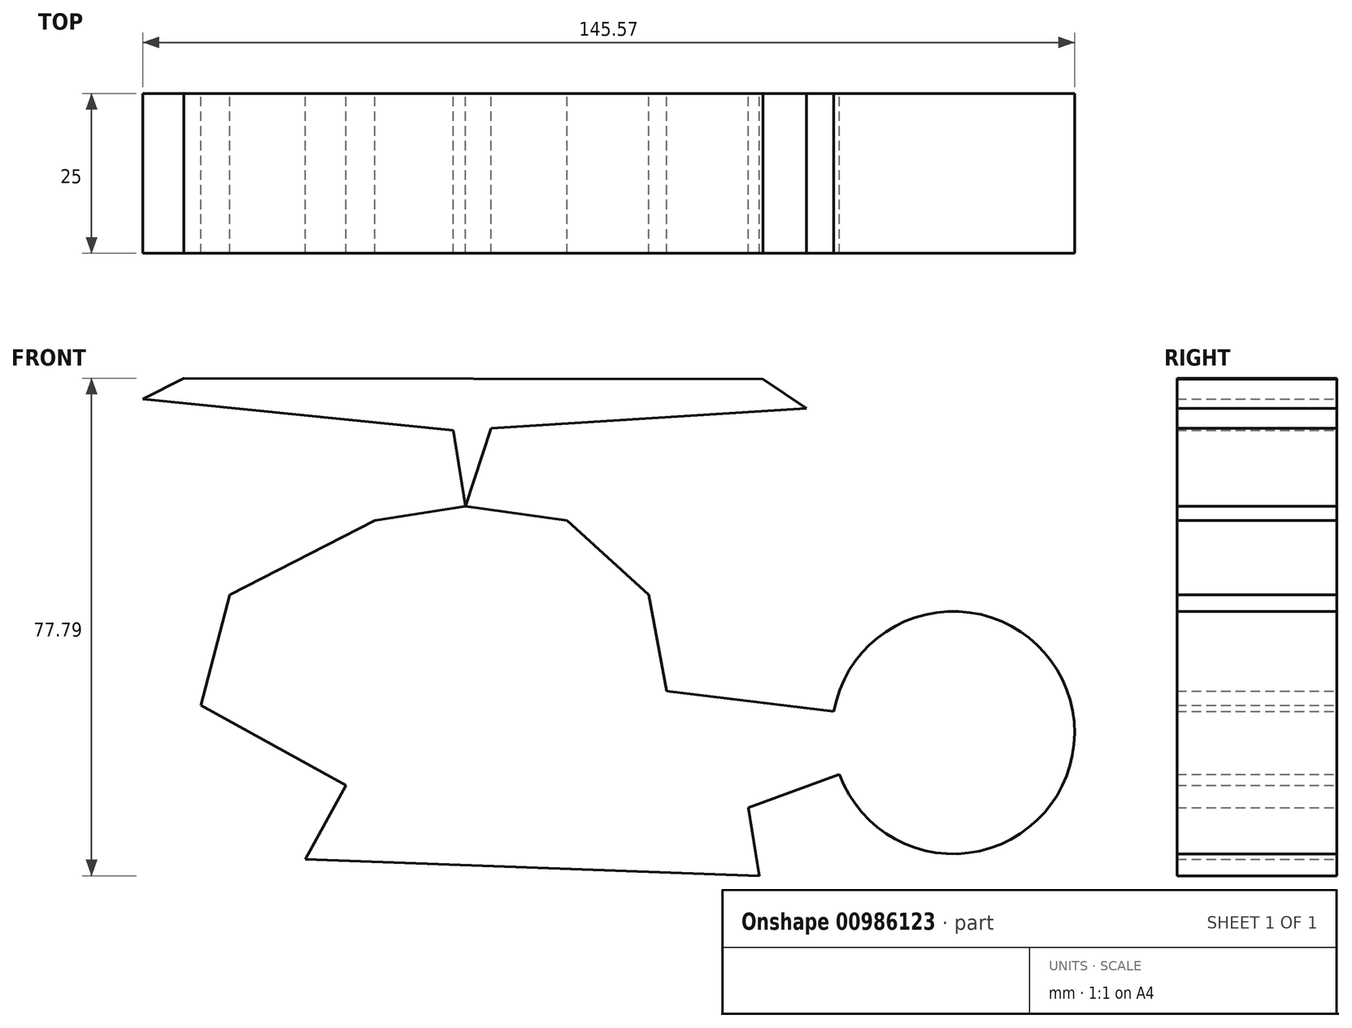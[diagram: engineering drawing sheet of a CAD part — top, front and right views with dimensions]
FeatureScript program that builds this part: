
annotation { "Feature Type Name" : "Feature", "Feature Type Description" : "" }
export const myFeature = defineFeature(function(context is Context, id is Id, definition is map)
    precondition{}
    {
        {
            var Q0;
            Q0=qCreatedBy(makeId("Front.planeOp"),FACE);
            var sketch = newSketch(context, id + "F0", { "sketchPlane" : qUnion([Q0])});
            skLineSegment(sketch, "E0", {"start": v(0, 0) * mm, "end": v(-29.04, 3.54) * mm});
            skLineSegment(sketch, "E1", {"start": v(-29.04, 3.54) * mm, "end": v(-51.7, 16) * mm});
            skLineSegment(sketch, "E2", {"start": v(-51.7, 16) * mm, "end": v(-47.17, 33.28) * mm});
            skLineSegment(sketch, "E3", {"start": v(-47.17, 33.28) * mm, "end": v(-24.5, 44.9) * mm});
            skLineSegment(sketch, "E4", {"start": v(-24.5, 44.9) * mm, "end": v(5.52, 44.9) * mm});
            skLineSegment(sketch, "E5", {"start": v(0, 0) * mm, "end": v(33.85, 0) * mm});
            skLineSegment(sketch, "E6", {"start": v(5.52, 44.9) * mm, "end": v(18.27, 33.28) * mm});
            skLineSegment(sketch, "E7", {"start": v(18.27, 33.28) * mm, "end": v(21.1, 18.27) * mm});
            skLineSegment(sketch, "E8", {"start": v(21.1, 18.27) * mm, "end": v(23.08, 7.79) * mm});
            skLineSegment(sketch, "E9", {"start": v(21.1, 18.27) * mm, "end": v(56.09, 14) * mm});
            skLineSegment(sketch, "E10", {"start": v(33.85, 0) * mm, "end": v(65.86, 11.76) * mm});
            skLineSegment(sketch, "E11", {"start": v(56.09, 14) * mm, "end": v(65.86, 11.76) * mm});
            skCircle(sketch, "E12", {"center": v(65.86, 11.76) * mm, "radius": 18.95 * mm});
            skLineSegment(sketch, "E13", {"start": v(-24.5, 44.9) * mm, "end": v(-10.34, 47.17) * mm});
            skLineSegment(sketch, "E14", {"start": v(-10.34, 47.17) * mm, "end": v(5.52, 44.9) * mm});
            skLineSegment(sketch, "E15", {"start": v(-10.34, 47.17) * mm, "end": v(-6.37, 59.35) * mm});
            skLineSegment(sketch, "E16", {"start": v(-10.34, 47.17) * mm, "end": v(-12.24, 59.02) * mm});
            skLineSegment(sketch, "E17", {"start": v(-6.37, 59.35) * mm, "end": v(42.92, 62.46) * mm});
            skLineSegment(sketch, "E18", {"start": v(-12.24, 59.02) * mm, "end": v(-60.76, 63.88) * mm});
            skLineSegment(sketch, "E19", {"start": v(-60.76, 63.88) * mm, "end": v(-54.33, 67.17) * mm});
            skLineSegment(sketch, "E20", {"start": v(42.92, 62.46) * mm, "end": v(36.12, 67) * mm});
            skLineSegment(sketch, "E21", {"start": v(-54.33, 67.17) * mm, "end": v(36.12, 67) * mm});
            skLineSegment(sketch, "E22", {"start": v(-29.04, 3.54) * mm, "end": v(-35.4, -8.03) * mm});
            skLineSegment(sketch, "E23", {"start": v(-35.4, -8.03) * mm, "end": v(35.55, -10.62) * mm});
            skLineSegment(sketch, "E24", {"start": v(35.55, -10.62) * mm, "end": v(33.85, 0) * mm});
            skSolve(sketch);
        }
        {
            var Q0;
            Q0 = qSketchRegion(id + "F0", true);
            extrude(context, id + "F1", {"entities" : qUnion([Q0]), "depth" : 25 * mm, "offsetDistance" : 25 * mm});
        }
    });
